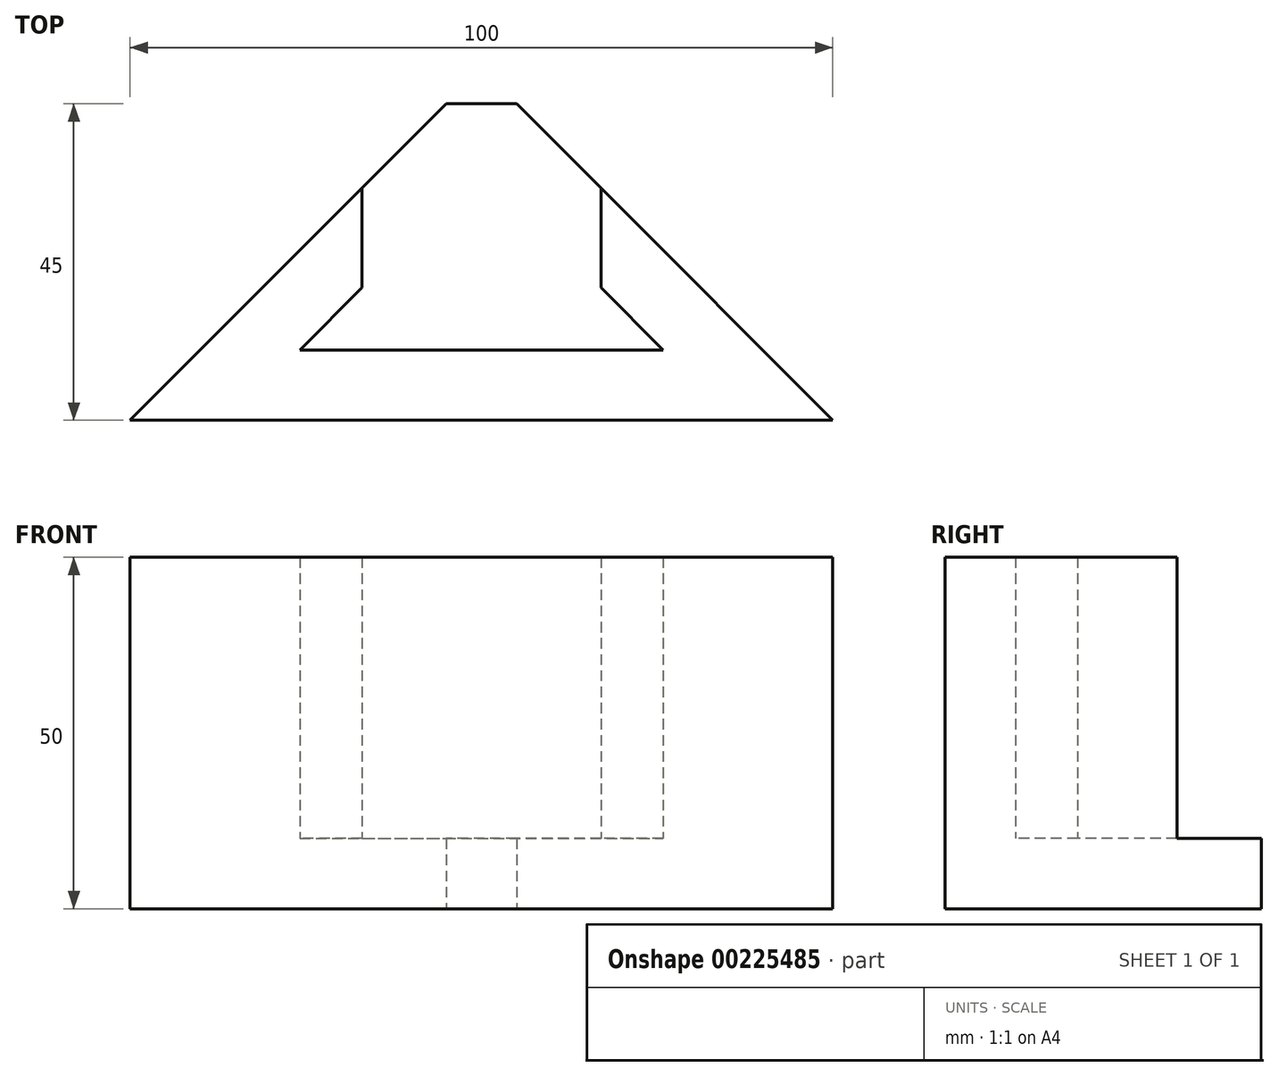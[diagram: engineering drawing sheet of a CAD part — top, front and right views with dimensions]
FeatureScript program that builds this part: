
annotation { "Feature Type Name" : "Feature", "Feature Type Description" : "" }
export const myFeature = defineFeature(function(context is Context, id is Id, definition is map)
    precondition{}
    {
        {
            var Q0;
            Q0=qCreatedBy(makeId("Top.planeOp"),FACE);
            var sketch = newSketch(context, id + "F0", { "sketchPlane" : qUnion([Q0])});
            skLineSegment(sketch, "E0", {"start": v(-50, -22.5) * mm, "end": v(50, -22.5) * mm});
            skLineSegment(sketch, "E1", {"start": v(50, -22.5) * mm, "end": v(5, 22.5) * mm});
            skLineSegment(sketch, "E2", {"start": v(5, 22.5) * mm, "end": v(-5, 22.5) * mm});
            skPoint(sketch, "E3", {"position": v(0, 0) * mm});
            skLineSegment(sketch, "E4", {"start": v(-50, -22.5) * mm, "end": v(-5, 22.5) * mm});
            skLineSegment(sketch, "E5", {"start": v(-27.5, 0) * mm, "end": v(27.5, 0) * mm, "construction": true});
            skLineSegment(sketch, "E6", {"start": v(0, -22.5) * mm, "end": v(0, 22.5) * mm, "construction": true});
            skSolve(sketch);
        }
        {
            var Q0;
            Q0=makeQuery(id+"F0.imprint","IMPRINT",FACE,{"disambiguationData":[TD([[makeQuery(id+"F0.imprint","IMPRINT",EDGE,{"derivedFrom":sQuery(id+"F0.wireOp",EDGE,"E0")}),1.0]])]});
            extrude(context, id + "F1", {"entities" : qUnion([Q0]), "offsetDistance" : 25 * mm, "depth" : 10 * mm});
        }
        {
            var Q0;
            Q0=makeQuery(id+"F1.opExtrude","CAP_FACE",FACE,{"disambiguationData":[OSD([sQuery(id+"F0.wireOp",EDGE,"E0"),sQuery(id+"F0.wireOp",EDGE,"E1"),sQuery(id+"F0.wireOp",EDGE,"E2"),sQuery(id+"F0.wireOp",EDGE,"x5c1i1SD-rFyp-DfRU-EHEr-BeWNeOyAB0PI")])],"isStart":false});
            var sketch = newSketch(context, id + "F2", { "sketchPlane" : qUnion([Q0])});
            skLineSegment(sketch, "E7", {"start": v(-25.86, -12.5) * mm, "end": v(25.86, -12.5) * mm});
            skLineSegment(sketch, "E8", {"start": v(17, 10.5) * mm, "end": v(50, -22.5) * mm});
            skLineSegment(sketch, "E9", {"start": v(50, -22.5) * mm, "end": v(-50, -22.5) * mm});
            skLineSegment(sketch, "E10", {"start": v(25.86, -12.5) * mm, "end": v(17, -3.64) * mm});
            skLineSegment(sketch, "E11", {"start": v(-17, -3.64) * mm, "end": v(-25.86, -12.5) * mm});
            skLineSegment(sketch, "E12", {"start": v(-17, 10.5) * mm, "end": v(-50, -22.5) * mm});
            skLineSegment(sketch, "E13", {"start": v(17, 10.5) * mm, "end": v(17, -3.64) * mm});
            skLineSegment(sketch, "E14", {"start": v(-17, 10.5) * mm, "end": v(-17, -3.64) * mm});
            skSolve(sketch);
        }
        {
            var Q0;
            Q0=makeQuery(id+"F2.imprint","IMPRINT",FACE,{"disambiguationData":[TD([[makeQuery(id+"F2.imprint","IMPRINT",EDGE,{"derivedFrom":sQuery(id+"F2.wireOp",EDGE,"E7")}),-1.0]])]});
            extrude(context, id + "F3", {"entities" : qUnion([Q0]), "operationType" : NewBodyOperationType.ADD, "depth" : 40 * mm});
        }
    });
